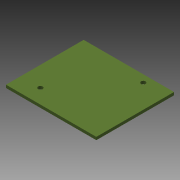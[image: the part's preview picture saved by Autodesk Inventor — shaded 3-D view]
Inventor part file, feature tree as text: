
AUTODESK INVENTOR PART (.ipt)
format: ipt  version: 2015 (Build 190159000, 159)  size: 79,872 bytes
history: native  units: mm
features: extrude x1, sketch x1
ambient origin geometry x8: Origin, YZ Plane, XZ Plane, XY Plane, X Axis, Y Axis, Z Axis, Center Point
bodies: Volumenkörper1 (feature_tree)
feature tree (2):
  extrude  "Extrusion1"  Depth=63.5mm
  sketch  "Skizze1"  dims[d0=54.6mm d1=63.5mm d2=3.2mm d3=3.2mm d4=14.0mm d5=10.2mm d6=49.5mm d7=47.0mm d8=2.0mm d9=0.0mm d10=33.0mm d11=39.3mm]
